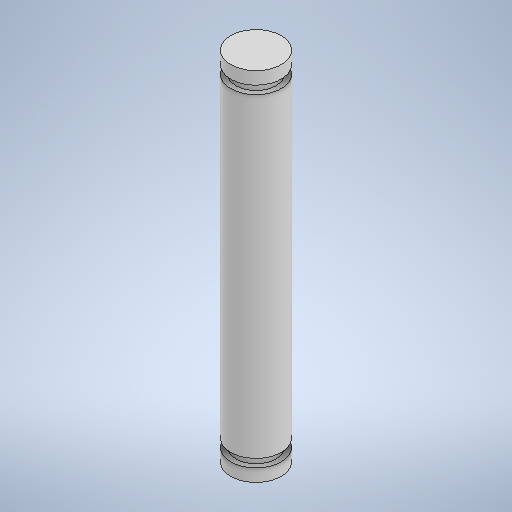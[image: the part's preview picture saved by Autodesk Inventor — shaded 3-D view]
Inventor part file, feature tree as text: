
AUTODESK INVENTOR PART (.ipt)
format: ipt  version: 2025 (Build 290162010, 162A)  size: 262,144 bytes
history: native  units: mm
features: revolve x1, sketch x1
ambient origin geometry x8: Origin, YZ Plane, XZ Plane, XY Plane, X Axis, Y Axis, Z Axis, Center Point
bodies: Volumenkörper1 (feature_tree)
feature tree (2):
  revolve  "Umdrehung1"
  sketch  "Skizze1"  dims[d0=2.0mm d1=1.0mm d2=0.65mm d3=0.65mm d5=1.0mm d6=4.0mm d7=3.2mm d8=90.0deg d9=25.0mm]
